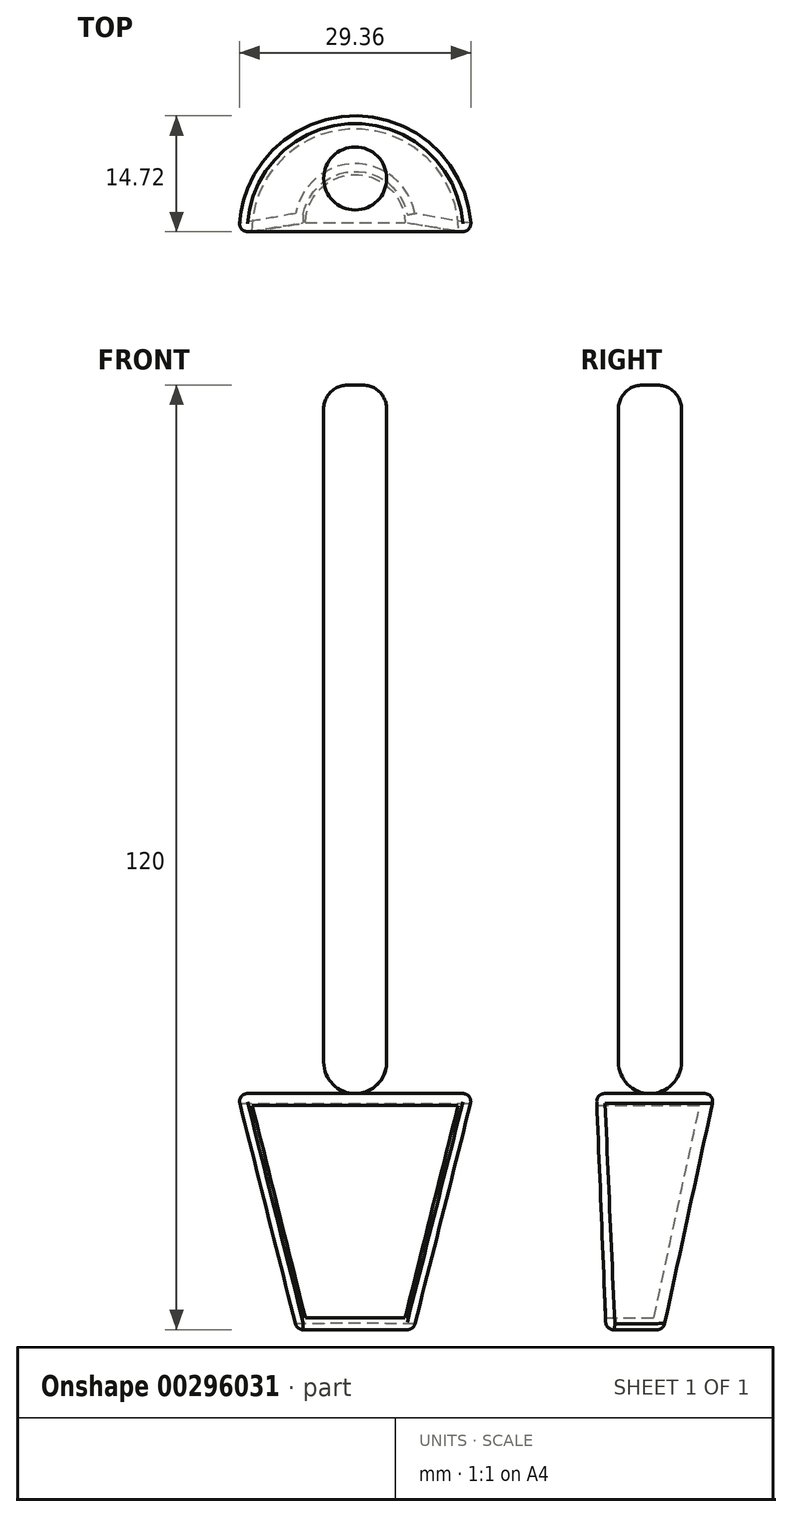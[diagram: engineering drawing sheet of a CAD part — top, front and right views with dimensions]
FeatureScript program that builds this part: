
annotation { "Feature Type Name" : "Feature", "Feature Type Description" : "" }
export const myFeature = defineFeature(function(context is Context, id is Id, definition is map)
    precondition{}
    {
        {
            var Q0;
            Q0=qCreatedBy(makeId("Top.planeOp"),FACE);
            var sketch = newSketch(context, id + "F0", { "sketchPlane" : qUnion([Q0])});
            skCircle(sketch, "E0", {"center": v(0, 0) * mm, "radius": 4 * mm});
            skSolve(sketch);
        }
        {
            var Q0;
            Q0 = qSketchRegion(id + "F0", true);
            extrude(context, id + "F1", {"entities" : qUnion([Q0]), "depth" : 90 * mm});
        }
        {
            var Q0;
            Q0=makeQuery(id+"F1.opExtrude","CAP_EDGE",EDGE,{"disambiguationData":[OSD([sQuery(id+"F0.wireOp",EDGE,"E0")])],"isStart":false});
            fillet(context, id + "F2", {"entities" : qUnion([Q0]), "radius" : 3 * mm, "tangentPropagation" : true, "allowEdgeOverflow" : false});
        }
        {
            var Q0;
            Q0=makeQuery(id+"F1.opExtrude","CAP_FACE",FACE,{"disambiguationData":[OSD([sQuery(id+"F0.wireOp",EDGE,"E0")])],"isStart":true});
            var sketch = newSketch(context, id + "F3", { "sketchPlane" : qUnion([Q0])});
            skLineSegment(sketch, "E1", {"start": v(0, 4) * mm, "end": v(15, 4) * mm});
            skLineSegment(sketch, "E2", {"start": v(0, 4) * mm, "end": v(-15, 4) * mm});
            skArc(sketch, "E3", {"start": v(-15, 4) * mm, "mid": v(0, -11) * mm, "end": v(15, 4) * mm});
            skSolve(sketch);
        }
        {
            var Q0;
            Q0=makeQuery(id+"F3.imprint","IMPRINT",FACE,{"disambiguationData":[TD([[makeQuery(id+"F3.imprint","IMPRINT",EDGE,{"derivedFrom":makeQuery(id+"F1.opExtrude","CAP_EDGE",EDGE,{"disambiguationData":[OSD([sQuery(id+"F0.wireOp",EDGE,"E0")])],"isStart":true})}),-1.0]])]});
            cPlane(context, id + "F4", {"entities" : qUnion([Q0]), "cplaneType" : CPlaneType.OFFSET, "offset" : 30 * mm, "width" : 150 * mm, "height" : 150 * mm});
        }
        {
            var Q0;
            Q0=qCreatedBy(id+"F4.planeOp",FACE);
            var sketch = newSketch(context, id + "F5", { "sketchPlane" : qUnion([Q0])});
            skLineSegment(sketch, "E4.0", {"start": v(0, 2.79) * mm, "end": v(7.5, 2.79) * mm});
            skArc(sketch, "E5.0", {"start": v(-7.5, 2.79) * mm, "mid": v(0, -4.5) * mm, "end": v(7.5, 2.79) * mm});
            skLineSegment(sketch, "E6.0", {"start": v(0, 2.79) * mm, "end": v(-7.5, 2.79) * mm});
            skSolve(sketch);
        }
        {
            var Q0;
            Q0 = qSketchRegion(id + "F3", true);
            var Q1;
            Q1 = qSketchRegion(id + "F5", true);
            loft(context, id + "F6", {"sheetProfilesArray" : [{ "sheetProfileEntities" : qUnion([Q0]) }, { "sheetProfileEntities" : qUnion([Q1]) }]});
        }
        {
            var Q0;
            Q0=makeQuery(id+"F6.opLoft","SWEPT_FACE",FACE,{"disambiguationData":[OSD([sQuery(id+"F0.wireOp",EDGE,"E0"),sQuery(id+"F3.wireOp",EDGE,"E1"),sQuery(id+"F3.wireOp",EDGE,"E2"),sQuery(id+"F3.wireOp",EDGE,"E3"),sQuery(id+"F5.wireOp",EDGE,"E4.0"),sQuery(id+"F5.wireOp",EDGE,"E5.0"),sQuery(id+"F5.wireOp",EDGE,"E6.0")])]});
            shell(context, id + "F7", {"entities" : qUnion([Q0]), "thickness" : 1.5 * mm});
        }
        {
            var Q0;
            Q0=makeQuery(id+"F6.opLoft","CAP_FACE",FACE,{"disambiguationData":[OSD([makeQuery(id+"F3.imprint","IMPRINT",FACE,{"disambiguationData":[TD([[makeQuery(id+"F3.imprint","IMPRINT",EDGE,{"derivedFrom":makeQuery(id+"F1.opExtrude","CAP_EDGE",EDGE,{"disambiguationData":[OSD([sQuery(id+"F0.wireOp",EDGE,"E0")])],"isStart":true})}),-1.0]])]})])],"isStart":true});
            var Q1;
            Q1=makeQuery(id+"F6.opLoft","CAP_FACE",FACE,{"disambiguationData":[OSD([makeQuery(id+"F5.imprint","IMPRINT",FACE,{"disambiguationData":[TD([[makeQuery(id+"F5.imprint","IMPRINT",EDGE,{"derivedFrom":sQuery(id+"F5.wireOp",EDGE,"E4.0")}),-1.0]])]})])],"isStart":true});
            var Q2;
            Q2=makeQuery(id+"F6.opLoft","SWEPT_EDGE",EDGE,{"disambiguationData":[OSD([sQuery(id+"F3.wireOp",EDGE,"E2"),sQuery(id+"F3.wireOp",EDGE,"E3"),sQuery(id+"F5.wireOp",EDGE,"E5.0"),sQuery(id+"F5.wireOp",EDGE,"E6.0")])]});
            var Q3;
            Q3=makeQuery(id+"F6.opLoft","SWEPT_EDGE",EDGE,{"disambiguationData":[OSD([sQuery(id+"F3.wireOp",EDGE,"E1"),sQuery(id+"F3.wireOp",EDGE,"E3"),sQuery(id+"F5.wireOp",EDGE,"E4.0"),sQuery(id+"F5.wireOp",EDGE,"E5.0")])]});
            fillet(context, id + "F8", {"entities" : qUnion([Q0, Q1, Q2, Q3]), "radius" : 1 * mm, "tangentPropagation" : true, "allowEdgeOverflow" : false});
        }
        {
            var Q0;
            Q0=makeQuery(id+"F6.opLoft","SWEPT_BODY",BODY,{"disambiguationData":[OSD([makeQuery(id+"F3.imprint","IMPRINT",FACE,{"disambiguationData":[TD([[makeQuery(id+"F3.imprint","IMPRINT",EDGE,{"derivedFrom":sQuery(id+"F3.wireOp",EDGE,"E1")}),-1.0]])]}),makeQuery(id+"F5.imprint","IMPRINT",FACE,{"disambiguationData":[TD([[makeQuery(id+"F5.imprint","IMPRINT",EDGE,{"derivedFrom":sQuery(id+"F5.wireOp",EDGE,"E4.0")}),-1.0]])]})])]});
            transform(context, id + "F9", {"entities" : qUnion([Q0]), "transformType" : TransformType.TRANSLATION_3D, "dx" : 0 * mm, "dy" : -0.5 * mm, "dz" : 0 * mm, "makeCopy" : false});
        }
        {
            var Q0;
            Q0=makeQuery(id+"F6.opLoft","SWEPT_BODY",BODY,{"disambiguationData":[OSD([makeQuery(id+"F3.imprint","IMPRINT",FACE,{"disambiguationData":[TD([[makeQuery(id+"F3.imprint","IMPRINT",EDGE,{"derivedFrom":sQuery(id+"F3.wireOp",EDGE,"E1")}),-1.0]])]}),makeQuery(id+"F5.imprint","IMPRINT",FACE,{"disambiguationData":[TD([[makeQuery(id+"F5.imprint","IMPRINT",EDGE,{"derivedFrom":sQuery(id+"F5.wireOp",EDGE,"E4.0")}),-1.0]])]})])]});
            transform(context, id + "F10", {"entities" : qUnion([Q0]), "transformType" : TransformType.TRANSLATION_3D, "dx" : 0 * mm, "dy" : -2.3 * mm, "dz" : 0 * mm, "makeCopy" : false});
        }
        {
            var Q0;
            Q0=makeQuery(id+"F1.opExtrude","CAP_EDGE",EDGE,{"disambiguationData":[OSD([sQuery(id+"F0.wireOp",EDGE,"E0")])],"isStart":true});
            fillet(context, id + "F11", {"entities" : qUnion([Q0]), "radius" : 4 * mm, "tangentPropagation" : true, "allowEdgeOverflow" : false});
        }
    });
